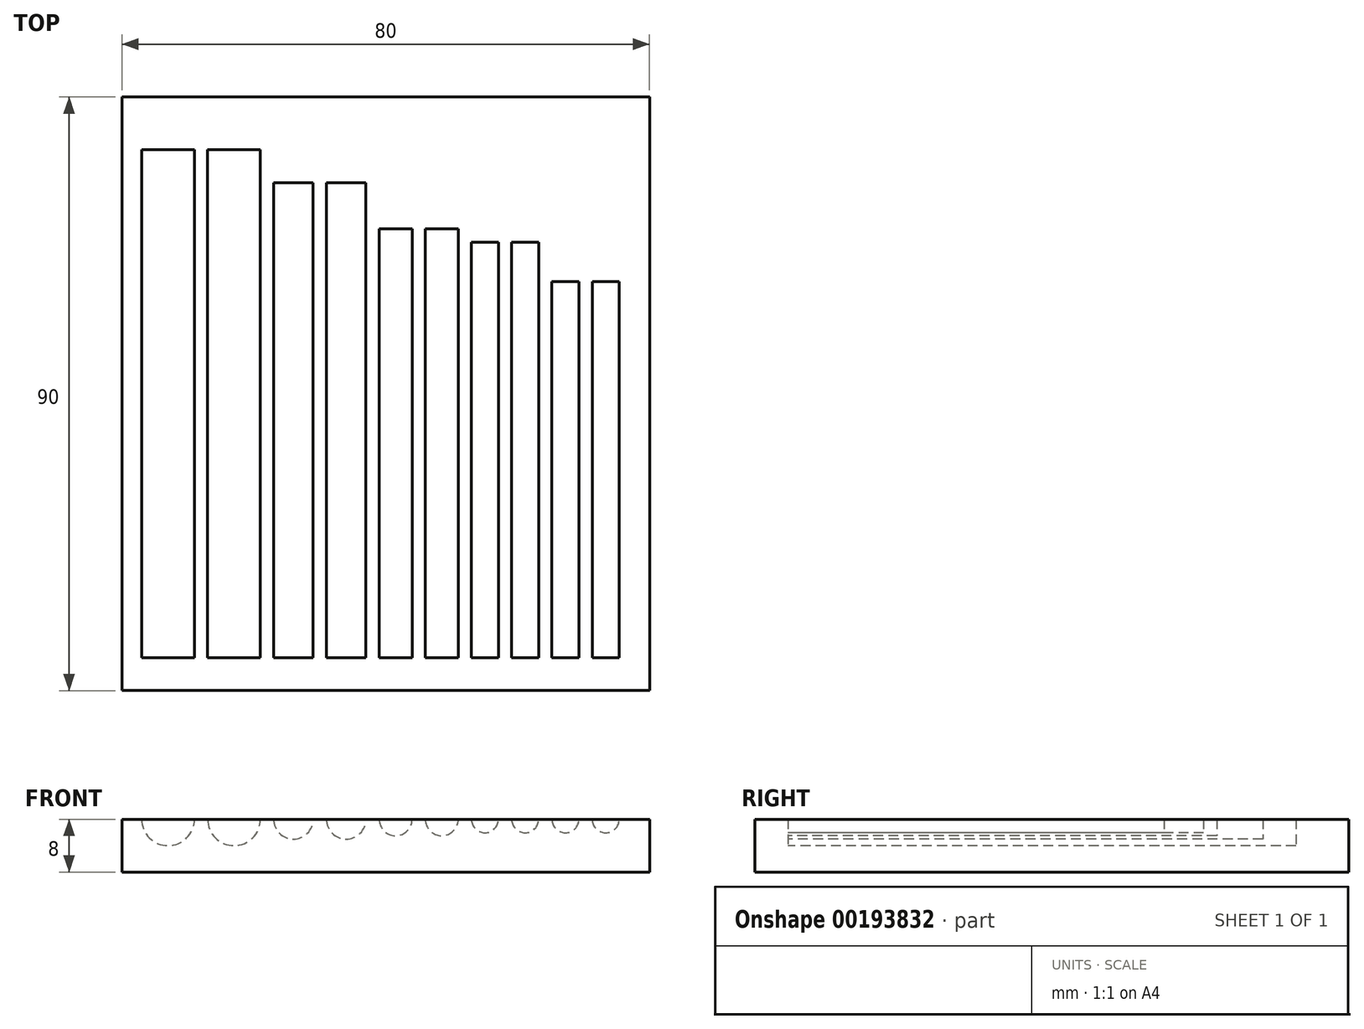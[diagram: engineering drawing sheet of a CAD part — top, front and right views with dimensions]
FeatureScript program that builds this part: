
annotation { "Feature Type Name" : "Feature", "Feature Type Description" : "" }
export const myFeature = defineFeature(function(context is Context, id is Id, definition is map)
    precondition{}
    {
        {
            var Q0;
            Q0=qCreatedBy(makeId("Top.planeOp"),FACE);
            var sketch = newSketch(context, id + "F0", { "sketchPlane" : qUnion([Q0])});
            skLineSegment(sketch, "E0.bottom", {"start": v(-60.82, 21.22) * mm, "end": v(19.18, 21.22) * mm});
            skLineSegment(sketch, "E0.top", {"start": v(-60.82, -68.78) * mm, "end": v(19.18, -68.78) * mm});
            skLineSegment(sketch, "E0.left", {"start": v(-60.82, 21.22) * mm, "end": v(-60.82, -68.78) * mm});
            skLineSegment(sketch, "E0.right", {"start": v(19.18, 21.22) * mm, "end": v(19.18, -68.78) * mm});
            skSolve(sketch);
        }
        {
            var Q0;
            Q0=makeQuery(id+"F0.imprint","IMPRINT",FACE,{"disambiguationData":[TD([[makeQuery(id+"F0.imprint","IMPRINT",EDGE,{"derivedFrom":sQuery(id+"F0.wireOp",EDGE,"E0.bottom")}),-1.0]])]});
            extrude(context, id + "F1", {"entities" : qUnion([Q0]), "depth" : 8 * mm});
        }
        {
            var Q0;
            Q0=makeQuery(id+"F1.opExtrude","SWEPT_FACE",FACE,{"disambiguationData":[OSD([sQuery(id+"F0.wireOp",EDGE,"E0.top")])]});
            var sketch = newSketch(context, id + "F2", { "sketchPlane" : qUnion([Q0])});
            skCircle(sketch, "E1", {"center": v(-53.82, 8) * mm, "radius": 4 * mm});
            skCircle(sketch, "E2.1.0.0", {"center": v(-43.82, 8) * mm, "radius": 4 * mm});
            skCircle(sketch, "E2.2.0.0", {"center": v(-34.82, 8) * mm, "radius": 3 * mm});
            skCircle(sketch, "E2.3.0.0", {"center": v(-26.82, 8) * mm, "radius": 3 * mm});
            skCircle(sketch, "E2.4.0.0", {"center": v(-19.32, 8) * mm, "radius": 2.5 * mm});
            skCircle(sketch, "E2.5.0.0", {"center": v(-12.32, 8) * mm, "radius": 2.5 * mm});
            skCircle(sketch, "E2.6.0.0", {"center": v(-5.77, 8) * mm, "radius": 2.05 * mm});
            skCircle(sketch, "E2.7.0.0", {"center": v(0.33, 8) * mm, "radius": 2.05 * mm});
            skCircle(sketch, "E2.8.0.0", {"center": v(6.43, 8) * mm, "radius": 2.05 * mm});
            skCircle(sketch, "E2.9.0.0", {"center": v(12.53, 8) * mm, "radius": 2.05 * mm});
            skLineSegment(sketch, "E2.direction1", {"start": v(-53.82, 8) * mm, "end": v(-43.82, 8) * mm, "construction": true});
            skSolve(sketch);
        }
        {
            var Q0;
            {var subQ0=sQuery(id+"F2.wireOp",EDGE,"E1");var subQ1=makeQuery(id+"F1.opExtrude","CAP_EDGE",EDGE,{"disambiguationData":[OSD([sQuery(id+"F0.wireOp",EDGE,"E0.top")])],"isStart":false});var subQ2=makeQuery(id+"F2.imprint","INTERSECT",VERTEX,{"disambiguationData":[OD(0.0)],"derivedFrom":[subQ1,subQ0]});Q0=makeQuery(id+"F2.imprint","IMPRINT",FACE,{"disambiguationData":[TD([[makeQuery(id+"F2.imprint","IMPRINT",EDGE,{"disambiguationData":[TD([[subQ2,-1.0]])],"derivedFrom":subQ0}),1.0]])]});}
            var Q1;
            {var subQ0=sQuery(id+"F2.wireOp",EDGE,"E2.1.0.0");var subQ1=makeQuery(id+"F1.opExtrude","CAP_EDGE",EDGE,{"disambiguationData":[OSD([sQuery(id+"F0.wireOp",EDGE,"E0.top")])],"isStart":false});var subQ2=makeQuery(id+"F2.imprint","INTERSECT",VERTEX,{"disambiguationData":[OD(0.0)],"derivedFrom":[subQ1,subQ0]});Q1=makeQuery(id+"F2.imprint","IMPRINT",FACE,{"disambiguationData":[TD([[makeQuery(id+"F2.imprint","IMPRINT",EDGE,{"disambiguationData":[TD([[subQ2,-1.0]])],"derivedFrom":subQ0}),1.0]])]});}
            extrude(context, id + "F3", {"entities" : qUnion([Q0, Q1]), "operationType" : NewBodyOperationType.REMOVE, "oppositeDirection" : true, "depth" : 82 * mm});
        }
        {
            var Q0;
            {var subQ0=sQuery(id+"F2.wireOp",EDGE,"E2.2.0.0");var subQ1=makeQuery(id+"F1.opExtrude","CAP_EDGE",EDGE,{"disambiguationData":[OSD([sQuery(id+"F0.wireOp",EDGE,"E0.top")])],"isStart":false});var subQ2=makeQuery(id+"F2.imprint","INTERSECT",VERTEX,{"disambiguationData":[OD(0.0)],"derivedFrom":[subQ1,subQ0]});Q0=makeQuery(id+"F2.imprint","IMPRINT",FACE,{"disambiguationData":[TD([[makeQuery(id+"F2.imprint","IMPRINT",EDGE,{"disambiguationData":[TD([[subQ2,-1.0]])],"derivedFrom":subQ0}),1.0]])]});}
            var Q1;
            {var subQ0=sQuery(id+"F2.wireOp",EDGE,"E2.3.0.0");var subQ1=makeQuery(id+"F1.opExtrude","CAP_EDGE",EDGE,{"disambiguationData":[OSD([sQuery(id+"F0.wireOp",EDGE,"E0.top")])],"isStart":false});var subQ2=makeQuery(id+"F2.imprint","INTERSECT",VERTEX,{"disambiguationData":[OD(0.0)],"derivedFrom":[subQ1,subQ0]});Q1=makeQuery(id+"F2.imprint","IMPRINT",FACE,{"disambiguationData":[TD([[makeQuery(id+"F2.imprint","IMPRINT",EDGE,{"disambiguationData":[TD([[subQ2,-1.0]])],"derivedFrom":subQ0}),1.0]])]});}
            extrude(context, id + "F4", {"entities" : qUnion([Q0, Q1]), "operationType" : NewBodyOperationType.REMOVE, "oppositeDirection" : true, "depth" : 77 * mm});
        }
        {
            var Q0;
            {var subQ0=sQuery(id+"F2.wireOp",EDGE,"E2.4.0.0");var subQ1=makeQuery(id+"F1.opExtrude","CAP_EDGE",EDGE,{"disambiguationData":[OSD([sQuery(id+"F0.wireOp",EDGE,"E0.top")])],"isStart":false});var subQ2=makeQuery(id+"F2.imprint","INTERSECT",VERTEX,{"disambiguationData":[OD(0.0)],"derivedFrom":[subQ1,subQ0]});Q0=makeQuery(id+"F2.imprint","IMPRINT",FACE,{"disambiguationData":[TD([[makeQuery(id+"F2.imprint","IMPRINT",EDGE,{"disambiguationData":[TD([[subQ2,-1.0]])],"derivedFrom":subQ0}),1.0]])]});}
            var Q1;
            {var subQ0=sQuery(id+"F2.wireOp",EDGE,"E2.5.0.0");var subQ1=makeQuery(id+"F1.opExtrude","CAP_EDGE",EDGE,{"disambiguationData":[OSD([sQuery(id+"F0.wireOp",EDGE,"E0.top")])],"isStart":false});var subQ2=makeQuery(id+"F2.imprint","INTERSECT",VERTEX,{"disambiguationData":[OD(0.0)],"derivedFrom":[subQ1,subQ0]});Q1=makeQuery(id+"F2.imprint","IMPRINT",FACE,{"disambiguationData":[TD([[makeQuery(id+"F2.imprint","IMPRINT",EDGE,{"disambiguationData":[TD([[subQ2,1.0]])],"derivedFrom":subQ0}),1.0]])]});}
            extrude(context, id + "F5", {"entities" : qUnion([Q0, Q1]), "operationType" : NewBodyOperationType.REMOVE, "oppositeDirection" : true, "depth" : 70 * mm});
        }
        {
            var Q0;
            {var subQ0=sQuery(id+"F2.wireOp",EDGE,"E2.6.0.0");var subQ1=makeQuery(id+"F1.opExtrude","CAP_EDGE",EDGE,{"disambiguationData":[OSD([sQuery(id+"F0.wireOp",EDGE,"E0.top")])],"isStart":false});var subQ2=makeQuery(id+"F2.imprint","INTERSECT",VERTEX,{"disambiguationData":[OD(0.0)],"derivedFrom":[subQ1,subQ0]});Q0=makeQuery(id+"F2.imprint","IMPRINT",FACE,{"disambiguationData":[TD([[makeQuery(id+"F2.imprint","IMPRINT",EDGE,{"disambiguationData":[TD([[subQ2,1.0]])],"derivedFrom":subQ0}),1.0]])]});}
            var Q1;
            {var subQ0=sQuery(id+"F2.wireOp",EDGE,"E2.7.0.0");var subQ1=makeQuery(id+"F1.opExtrude","CAP_EDGE",EDGE,{"disambiguationData":[OSD([sQuery(id+"F0.wireOp",EDGE,"E0.top")])],"isStart":false});var subQ2=makeQuery(id+"F2.imprint","INTERSECT",VERTEX,{"disambiguationData":[OD(0.0)],"derivedFrom":[subQ1,subQ0]});Q1=makeQuery(id+"F2.imprint","IMPRINT",FACE,{"disambiguationData":[TD([[makeQuery(id+"F2.imprint","IMPRINT",EDGE,{"disambiguationData":[TD([[subQ2,1.0]])],"derivedFrom":subQ0}),1.0]])]});}
            extrude(context, id + "F6", {"entities" : qUnion([Q0, Q1]), "operationType" : NewBodyOperationType.REMOVE, "oppositeDirection" : true, "depth" : 68 * mm});
        }
        {
            var Q0;
            {var subQ0=sQuery(id+"F2.wireOp",EDGE,"E2.8.0.0");var subQ1=makeQuery(id+"F1.opExtrude","CAP_EDGE",EDGE,{"disambiguationData":[OSD([sQuery(id+"F0.wireOp",EDGE,"E0.top")])],"isStart":false});var subQ2=makeQuery(id+"F2.imprint","INTERSECT",VERTEX,{"disambiguationData":[OD(0.0)],"derivedFrom":[subQ1,subQ0]});Q0=makeQuery(id+"F2.imprint","IMPRINT",FACE,{"disambiguationData":[TD([[makeQuery(id+"F2.imprint","IMPRINT",EDGE,{"disambiguationData":[TD([[subQ2,1.0]])],"derivedFrom":subQ0}),1.0]])]});}
            var Q1;
            {var subQ0=sQuery(id+"F2.wireOp",EDGE,"E2.9.0.0");var subQ1=makeQuery(id+"F1.opExtrude","CAP_EDGE",EDGE,{"disambiguationData":[OSD([sQuery(id+"F0.wireOp",EDGE,"E0.top")])],"isStart":false});var subQ2=makeQuery(id+"F2.imprint","INTERSECT",VERTEX,{"disambiguationData":[OD(0.0)],"derivedFrom":[subQ1,subQ0]});Q1=makeQuery(id+"F2.imprint","IMPRINT",FACE,{"disambiguationData":[TD([[makeQuery(id+"F2.imprint","IMPRINT",EDGE,{"disambiguationData":[TD([[subQ2,1.0]])],"derivedFrom":subQ0}),1.0]])]});}
            extrude(context, id + "F7", {"entities" : qUnion([Q0, Q1]), "operationType" : NewBodyOperationType.REMOVE, "oppositeDirection" : true, "depth" : 62 * mm});
        }
        {
            var Q0;
            {var subQ0=sQuery(id+"F2.wireOp",EDGE,"E1");var subQ1=makeQuery(id+"F1.opExtrude","CAP_EDGE",EDGE,{"disambiguationData":[OSD([sQuery(id+"F0.wireOp",EDGE,"E0.top")])],"isStart":false});var subQ2=makeQuery(id+"F2.imprint","INTERSECT",VERTEX,{"disambiguationData":[OD(0.0)],"derivedFrom":[subQ1,subQ0]});Q0=makeQuery(id+"F2.imprint","IMPRINT",FACE,{"disambiguationData":[TD([[makeQuery(id+"F2.imprint","IMPRINT",EDGE,{"disambiguationData":[TD([[subQ2,-1.0]])],"derivedFrom":subQ0}),1.0]])]});}
            var Q1;
            {var subQ0=sQuery(id+"F2.wireOp",EDGE,"E2.1.0.0");var subQ1=makeQuery(id+"F1.opExtrude","CAP_EDGE",EDGE,{"disambiguationData":[OSD([sQuery(id+"F0.wireOp",EDGE,"E0.top")])],"isStart":false});var subQ2=makeQuery(id+"F2.imprint","INTERSECT",VERTEX,{"disambiguationData":[OD(0.0)],"derivedFrom":[subQ1,subQ0]});Q1=makeQuery(id+"F2.imprint","IMPRINT",FACE,{"disambiguationData":[TD([[makeQuery(id+"F2.imprint","IMPRINT",EDGE,{"disambiguationData":[TD([[subQ2,-1.0]])],"derivedFrom":subQ0}),1.0]])]});}
            var Q2;
            {var subQ0=sQuery(id+"F2.wireOp",EDGE,"E2.2.0.0");var subQ1=makeQuery(id+"F1.opExtrude","CAP_EDGE",EDGE,{"disambiguationData":[OSD([sQuery(id+"F0.wireOp",EDGE,"E0.top")])],"isStart":false});var subQ2=makeQuery(id+"F2.imprint","INTERSECT",VERTEX,{"disambiguationData":[OD(0.0)],"derivedFrom":[subQ1,subQ0]});Q2=makeQuery(id+"F2.imprint","IMPRINT",FACE,{"disambiguationData":[TD([[makeQuery(id+"F2.imprint","IMPRINT",EDGE,{"disambiguationData":[TD([[subQ2,-1.0]])],"derivedFrom":subQ0}),1.0]])]});}
            var Q3;
            {var subQ0=sQuery(id+"F2.wireOp",EDGE,"E2.3.0.0");var subQ1=makeQuery(id+"F1.opExtrude","CAP_EDGE",EDGE,{"disambiguationData":[OSD([sQuery(id+"F0.wireOp",EDGE,"E0.top")])],"isStart":false});var subQ2=makeQuery(id+"F2.imprint","INTERSECT",VERTEX,{"disambiguationData":[OD(0.0)],"derivedFrom":[subQ1,subQ0]});Q3=makeQuery(id+"F2.imprint","IMPRINT",FACE,{"disambiguationData":[TD([[makeQuery(id+"F2.imprint","IMPRINT",EDGE,{"disambiguationData":[TD([[subQ2,-1.0]])],"derivedFrom":subQ0}),1.0]])]});}
            var Q4;
            {var subQ0=sQuery(id+"F2.wireOp",EDGE,"E2.4.0.0");var subQ1=makeQuery(id+"F1.opExtrude","CAP_EDGE",EDGE,{"disambiguationData":[OSD([sQuery(id+"F0.wireOp",EDGE,"E0.top")])],"isStart":false});var subQ2=makeQuery(id+"F2.imprint","INTERSECT",VERTEX,{"disambiguationData":[OD(0.0)],"derivedFrom":[subQ1,subQ0]});Q4=makeQuery(id+"F2.imprint","IMPRINT",FACE,{"disambiguationData":[TD([[makeQuery(id+"F2.imprint","IMPRINT",EDGE,{"disambiguationData":[TD([[subQ2,-1.0]])],"derivedFrom":subQ0}),1.0]])]});}
            var Q5;
            {var subQ0=sQuery(id+"F2.wireOp",EDGE,"E2.5.0.0");var subQ1=makeQuery(id+"F1.opExtrude","CAP_EDGE",EDGE,{"disambiguationData":[OSD([sQuery(id+"F0.wireOp",EDGE,"E0.top")])],"isStart":false});var subQ2=makeQuery(id+"F2.imprint","INTERSECT",VERTEX,{"disambiguationData":[OD(0.0)],"derivedFrom":[subQ1,subQ0]});Q5=makeQuery(id+"F2.imprint","IMPRINT",FACE,{"disambiguationData":[TD([[makeQuery(id+"F2.imprint","IMPRINT",EDGE,{"disambiguationData":[TD([[subQ2,1.0]])],"derivedFrom":subQ0}),1.0]])]});}
            var Q6;
            {var subQ0=sQuery(id+"F2.wireOp",EDGE,"E2.6.0.0");var subQ1=makeQuery(id+"F1.opExtrude","CAP_EDGE",EDGE,{"disambiguationData":[OSD([sQuery(id+"F0.wireOp",EDGE,"E0.top")])],"isStart":false});var subQ2=makeQuery(id+"F2.imprint","INTERSECT",VERTEX,{"disambiguationData":[OD(0.0)],"derivedFrom":[subQ1,subQ0]});Q6=makeQuery(id+"F2.imprint","IMPRINT",FACE,{"disambiguationData":[TD([[makeQuery(id+"F2.imprint","IMPRINT",EDGE,{"disambiguationData":[TD([[subQ2,1.0]])],"derivedFrom":subQ0}),1.0]])]});}
            var Q7;
            {var subQ0=sQuery(id+"F2.wireOp",EDGE,"E2.7.0.0");var subQ1=makeQuery(id+"F1.opExtrude","CAP_EDGE",EDGE,{"disambiguationData":[OSD([sQuery(id+"F0.wireOp",EDGE,"E0.top")])],"isStart":false});var subQ2=makeQuery(id+"F2.imprint","INTERSECT",VERTEX,{"disambiguationData":[OD(0.0)],"derivedFrom":[subQ1,subQ0]});Q7=makeQuery(id+"F2.imprint","IMPRINT",FACE,{"disambiguationData":[TD([[makeQuery(id+"F2.imprint","IMPRINT",EDGE,{"disambiguationData":[TD([[subQ2,1.0]])],"derivedFrom":subQ0}),1.0]])]});}
            var Q8;
            {var subQ0=sQuery(id+"F2.wireOp",EDGE,"E2.8.0.0");var subQ1=makeQuery(id+"F1.opExtrude","CAP_EDGE",EDGE,{"disambiguationData":[OSD([sQuery(id+"F0.wireOp",EDGE,"E0.top")])],"isStart":false});var subQ2=makeQuery(id+"F2.imprint","INTERSECT",VERTEX,{"disambiguationData":[OD(0.0)],"derivedFrom":[subQ1,subQ0]});Q8=makeQuery(id+"F2.imprint","IMPRINT",FACE,{"disambiguationData":[TD([[makeQuery(id+"F2.imprint","IMPRINT",EDGE,{"disambiguationData":[TD([[subQ2,1.0]])],"derivedFrom":subQ0}),1.0]])]});}
            var Q9;
            {var subQ0=sQuery(id+"F2.wireOp",EDGE,"E2.9.0.0");var subQ1=makeQuery(id+"F1.opExtrude","CAP_EDGE",EDGE,{"disambiguationData":[OSD([sQuery(id+"F0.wireOp",EDGE,"E0.top")])],"isStart":false});var subQ2=makeQuery(id+"F2.imprint","INTERSECT",VERTEX,{"disambiguationData":[OD(0.0)],"derivedFrom":[subQ1,subQ0]});Q9=makeQuery(id+"F2.imprint","IMPRINT",FACE,{"disambiguationData":[TD([[makeQuery(id+"F2.imprint","IMPRINT",EDGE,{"disambiguationData":[TD([[subQ2,1.0]])],"derivedFrom":subQ0}),1.0]])]});}
            extrude(context, id + "F8", {"entities" : qUnion([Q0, Q1, Q2, Q3, Q4, Q5, Q6, Q7, Q8, Q9]), "operationType" : NewBodyOperationType.ADD, "oppositeDirection" : true, "depth" : 5 * mm});
        }
    });
